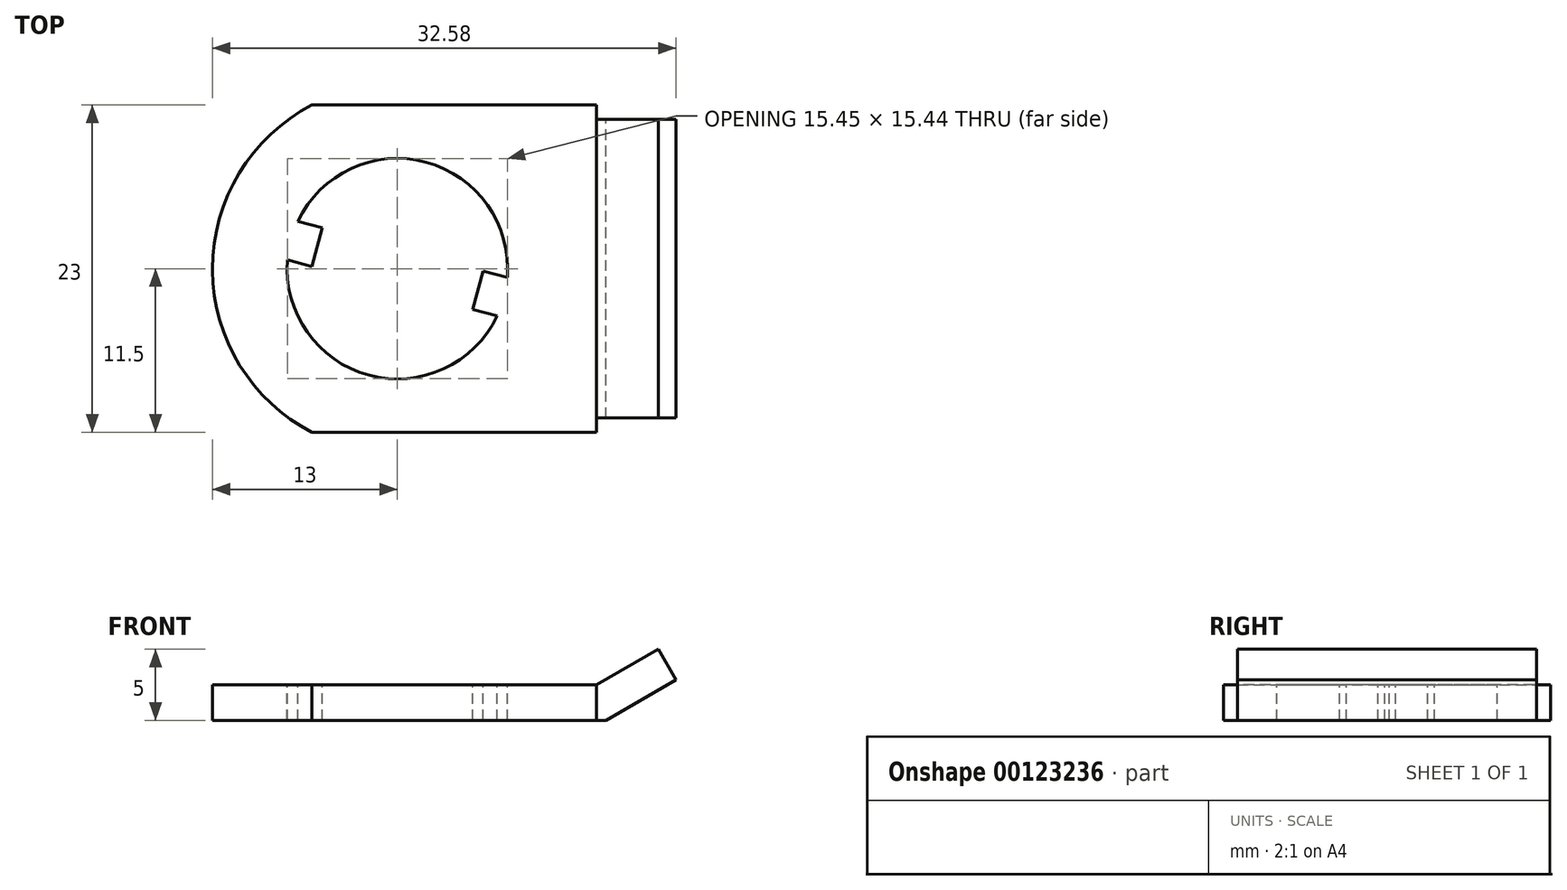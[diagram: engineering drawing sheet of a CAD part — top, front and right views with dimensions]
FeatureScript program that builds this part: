
annotation { "Feature Type Name" : "Feature", "Feature Type Description" : "" }
export const myFeature = defineFeature(function(context is Context, id is Id, definition is map)
    precondition{}
    {
        {
            var Q0;
            Q0=qCreatedBy(makeId("Front.planeOp"),FACE);
            var sketch = newSketch(context, id + "F0", { "sketchPlane" : qUnion([Q0])});
            skLineSegment(sketch, "E0.bottom", {"start": v(0, 0) * mm, "end": v(-27, 0) * mm});
            skLineSegment(sketch, "E0.top", {"start": v(0, -2.5) * mm, "end": v(-27, -2.5) * mm});
            skLineSegment(sketch, "E0.right", {"start": v(-27, 0) * mm, "end": v(-27, -2.5) * mm});
            skLineSegment(sketch, "E1", {"start": v(0, 0) * mm, "end": v(4.33, 2.5) * mm});
            skLineSegment(sketch, "E2", {"start": v(4.33, 2.5) * mm, "end": v(5.58, 0.33) * mm});
            skLineSegment(sketch, "E3", {"start": v(5.58, 0.33) * mm, "end": v(0.67, -2.5) * mm});
            skLineSegment(sketch, "E4", {"start": v(0, -2.5) * mm, "end": v(0.67, -2.5) * mm});
            skSolve(sketch);
        }
        {
            var Q0;
            Q0 = qSketchRegion(id + "F0", true);
            extrude(context, id + "F1", {"entities" : qUnion([Q0]), "endBound" : BoundingType.SYMMETRIC, "depth" : 23 * mm});
        }
        {
            var Q0;
            Q0=makeQuery(id+"F1.opExtrude","SWEPT_FACE",FACE,{"disambiguationData":[OSD([sQuery(id+"F0.wireOp",EDGE,"E0.bottom")])]});
            var sketch = newSketch(context, id + "F2", { "sketchPlane" : qUnion([Q0])});
            skArc(sketch, "E5", {"start": v(-21.73, 0.62) * mm, "mid": v(-16, -7.49) * mm, "end": v(-7, -3.33) * mm});
            skArc(sketch, "E6", {"start": v(-27, 0) * mm, "mid": v(-25.13, -6.74) * mm, "end": v(-20, -11.5) * mm});
            skArc(sketch, "E7", {"start": v(-20, 11.5) * mm, "mid": v(-27, 0) * mm, "end": v(-20, -11.5) * mm});
            skLineSegment(sketch, "E8.0", {"start": v(-21, 3.33) * mm, "end": v(-19.3, 2.87) * mm});
            skLineSegment(sketch, "E9.0", {"start": v(-21.73, 0.62) * mm, "end": v(-20.02, 0.16) * mm});
            skLineSegment(sketch, "E10", {"start": v(-19.3, 2.87) * mm, "end": v(-20.02, 0.16) * mm});
            skLineSegment(sketch, "E11.0", {"start": v(-8.7, -2.87) * mm, "end": v(-7, -3.33) * mm});
            skLineSegment(sketch, "E12.0", {"start": v(-7.98, -0.16) * mm, "end": v(-6.27, -0.62) * mm});
            skLineSegment(sketch, "E13", {"start": v(-7.98, -0.16) * mm, "end": v(-8.7, -2.87) * mm});
            skArc(sketch, "E14.trimOffspring", {"start": v(-6.27, -0.62) * mm, "mid": v(-12, 7.49) * mm, "end": v(-21, 3.33) * mm});
            skSolve(sketch);
        }
        {
            var Q0;
            {var subQ0=sQuery(id+"F2.wireOp",EDGE,"E6");var subQ1=makeQuery(id+"F1.opExtrude","SWEPT_EDGE",EDGE,{"disambiguationData":[OSD([sQuery(id+"F0.wireOp",EDGE,"E0.bottom"),sQuery(id+"F0.wireOp",EDGE,"E0.right")])]});var subQ3=makeQuery(id+"F2.imprint","INTERSECT",VERTEX,{"derivedFrom":[subQ1,subQ0]});Q0=makeQuery(id+"F2.imprint","IMPRINT",FACE,{"disambiguationData":[TD([[makeQuery(id+"F2.imprint","IMPRINT",EDGE,{"disambiguationData":[TD([[subQ3,1.0]])],"derivedFrom":subQ0}),1.0]])]});}
            var Q1;
            {var subQ0=sQuery(id+"F2.wireOp",EDGE,"E7");var subQ1=sQuery(id+"F2.wireOp",EDGE,"E6");var subQ2=sQuery(id+"F0.wireOp",EDGE,"E0.bottom");var subQ3=makeQuery(id+"F2.imprint","INTERSECT",VERTEX,{"derivedFrom":[makeQuery(id+"F1.opExtrude","CAP_EDGE",EDGE,{"disambiguationData":[OSD([subQ2])],"isStart":false}),subQ1,subQ0]});Q1=makeQuery(id+"F2.imprint","IMPRINT",FACE,{"disambiguationData":[TD([[makeQuery(id+"F2.imprint","IMPRINT",EDGE,{"disambiguationData":[TD([[subQ3,1.0]])],"derivedFrom":subQ1}),1.0]])]});}
            var Q2;
            {var subQ0=sQuery(id+"F2.wireOp",EDGE,"E7");var subQ1=sQuery(id+"F0.wireOp",EDGE,"E0.bottom");var subQ4=makeQuery(id+"F1.opExtrude","CAP_EDGE",EDGE,{"disambiguationData":[OSD([subQ1])],"isStart":true});var subQ5=makeQuery(id+"F2.imprint","INTERSECT",VERTEX,{"derivedFrom":[subQ4,subQ0]});Q2=makeQuery(id+"F2.imprint","IMPRINT",FACE,{"disambiguationData":[TD([[makeQuery(id+"F2.imprint","IMPRINT",EDGE,{"disambiguationData":[TD([[subQ5,-1.0]])],"derivedFrom":subQ4}),1.0]])]});}
            var Q3;
            {var subQ0=sQuery(id+"F2.wireOp",EDGE,"E6");var subQ1=sQuery(id+"F0.wireOp",EDGE,"E0.bottom");var subQ2=makeQuery(id+"F1.opExtrude","CAP_EDGE",EDGE,{"disambiguationData":[OSD([subQ1])],"isStart":false});var subQ3=makeQuery(id+"F2.imprint","INTERSECT",VERTEX,{"derivedFrom":[subQ2,subQ0,sQuery(id+"F2.wireOp",EDGE,"E7")]});Q3=makeQuery(id+"F2.imprint","IMPRINT",FACE,{"disambiguationData":[TD([[makeQuery(id+"F2.imprint","IMPRINT",EDGE,{"disambiguationData":[TD([[subQ3,1.0]])],"derivedFrom":subQ0}),-1.0]])]});}
            var Q4;
            Q4=makeQuery(id+"F2.imprint","IMPRINT",FACE,{"disambiguationData":[TD([[makeQuery(id+"F2.imprint","IMPRINT",EDGE,{"derivedFrom":sQuery(id+"F2.wireOp",EDGE,"E5")}),1.0]])]});
            extrude(context, id + "F3", {"entities" : qUnion([Q0, Q1, Q2, Q3, Q4]), "operationType" : NewBodyOperationType.REMOVE, "oppositeDirection" : true, "depth" : 25 * mm});
        }
        {
            var Q0;
            Q0=makeQuery(id+"F1.opExtrude","CAP_FACE",FACE,{"disambiguationData":[OSD([sQuery(id+"F0.wireOp",EDGE,"E0.bottom"),sQuery(id+"F0.wireOp",EDGE,"E0.top"),sQuery(id+"F0.wireOp",EDGE,"E0.right"),sQuery(id+"F0.wireOp",EDGE,"E1"),sQuery(id+"F0.wireOp",EDGE,"E2"),sQuery(id+"F0.wireOp",EDGE,"E3"),sQuery(id+"F0.wireOp",EDGE,"E4")])],"isStart":false});
            var sketch = newSketch(context, id + "F4", { "sketchPlane" : qUnion([Q0])});
            skLineSegment(sketch, "E15", {"start": v(0, 0) * mm, "end": v(0, -2.5) * mm});
            skLineSegment(sketch, "E16", {"start": v(0, -2.5) * mm, "end": v(0.67, -2.5) * mm});
            skLineSegment(sketch, "E17", {"start": v(0.67, -2.5) * mm, "end": v(5.58, 0.33) * mm});
            skLineSegment(sketch, "E18", {"start": v(5.58, 0.33) * mm, "end": v(4.33, 2.5) * mm});
            skLineSegment(sketch, "E19", {"start": v(4.33, 2.5) * mm, "end": v(0, 0) * mm});
            skSolve(sketch);
        }
        {
            var Q0;
            Q0=makeQuery(id+"F4.imprint","IMPRINT",FACE,{"disambiguationData":[TD([[makeQuery(id+"F4.imprint","IMPRINT",EDGE,{"derivedFrom":sQuery(id+"F4.wireOp",EDGE,"E15")}),1.0]])]});
            extrude(context, id + "F5", {"entities" : qUnion([Q0]), "operationType" : NewBodyOperationType.REMOVE, "oppositeDirection" : true, "depth" : 1 * mm});
        }
        {
            var Q0;
            Q0=makeQuery(id+"F1.opExtrude","CAP_FACE",FACE,{"disambiguationData":[OSD([sQuery(id+"F0.wireOp",EDGE,"E0.bottom"),sQuery(id+"F0.wireOp",EDGE,"E0.top"),sQuery(id+"F0.wireOp",EDGE,"E0.right"),sQuery(id+"F0.wireOp",EDGE,"E1"),sQuery(id+"F0.wireOp",EDGE,"E2"),sQuery(id+"F0.wireOp",EDGE,"E3"),sQuery(id+"F0.wireOp",EDGE,"E4")])],"isStart":true});
            var sketch = newSketch(context, id + "F6", { "sketchPlane" : qUnion([Q0])});
            skLineSegment(sketch, "E20", {"start": v(0, 0) * mm, "end": v(0, -2.5) * mm});
            skLineSegment(sketch, "E21", {"start": v(0, -2.5) * mm, "end": v(-0.67, -2.5) * mm});
            skLineSegment(sketch, "E22", {"start": v(-0.67, -2.5) * mm, "end": v(-5.58, 0.33) * mm});
            skLineSegment(sketch, "E23", {"start": v(-5.58, 0.33) * mm, "end": v(-4.33, 2.5) * mm});
            skLineSegment(sketch, "E24", {"start": v(-4.33, 2.5) * mm, "end": v(0, 0) * mm});
            skSolve(sketch);
        }
        {
            var Q0;
            Q0=makeQuery(id+"F6.imprint","IMPRINT",FACE,{"disambiguationData":[TD([[makeQuery(id+"F6.imprint","IMPRINT",EDGE,{"derivedFrom":sQuery(id+"F6.wireOp",EDGE,"E20")}),-1.0]])]});
            extrude(context, id + "F7", {"entities" : qUnion([Q0]), "operationType" : NewBodyOperationType.REMOVE, "oppositeDirection" : true, "depth" : 1 * mm});
        }
        {
            var Q0;
            Q0=makeQuery(id+"F2.imprint","IMPRINT",FACE,{"disambiguationData":[TD([[makeQuery(id+"F2.imprint","IMPRINT",EDGE,{"derivedFrom":sQuery(id+"F2.wireOp",EDGE,"E5")}),1.0]])]});
            extrude(context, id + "F8", {"entities" : qUnion([Q0]), "operationType" : NewBodyOperationType.REMOVE, "oppositeDirection" : true, "depth" : 25 * mm});
        }
    });
